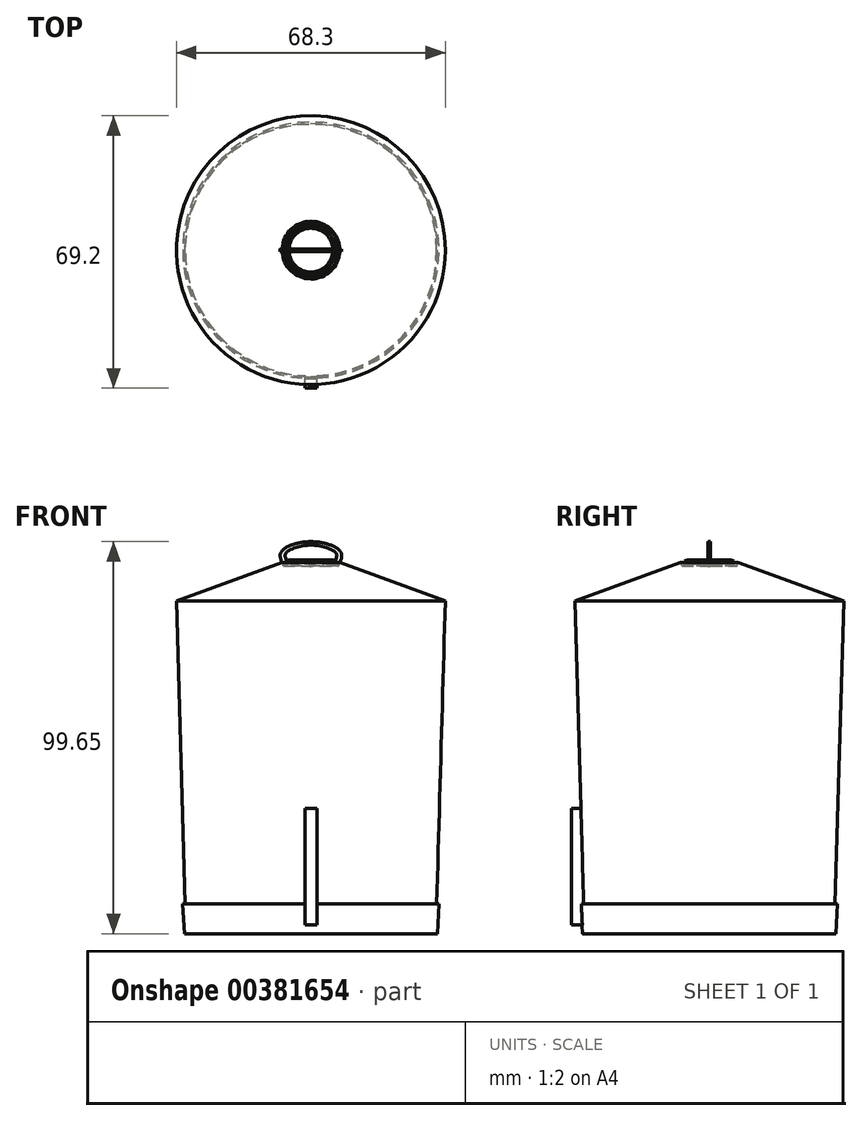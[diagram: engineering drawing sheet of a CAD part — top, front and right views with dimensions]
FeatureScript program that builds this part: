
annotation { "Feature Type Name" : "Feature", "Feature Type Description" : "" }
export const myFeature = defineFeature(function(context is Context, id is Id, definition is map)
    precondition{}
    {
        {
            var Q0;
            Q0=qCreatedBy(makeId("Front.planeOp"),FACE);
            var sketch = newSketch(context, id + "F0", { "sketchPlane" : qUnion([Q0])});
            skLineSegment(sketch, "E0", {"start": v(0, -43.36) * mm, "end": v(31.73, -43.36) * mm});
            skLineSegment(sketch, "E1", {"start": v(31.73, -43.36) * mm, "end": v(34.15, 41.18) * mm});
            skLineSegment(sketch, "E2", {"start": v(34.15, 41.18) * mm, "end": v(0, 41.18) * mm});
            skLineSegment(sketch, "E3", {"start": v(0, 53.72) * mm, "end": v(0, -61.04) * mm, "construction": true});
            skLineSegment(sketch, "E4", {"start": v(0, 41.18) * mm, "end": v(0, -43.36) * mm});
            skLineSegment(sketch, "E5", {"start": v(34.15, 41.18) * mm, "end": v(5.56, 51.68) * mm});
            skFitSpline(sketch, "E6", {"points": [v(5.56, 51.68) * mm, v(3.9, 50.72) * mm, v(1.74, 50.23) * mm, v(0, 50) * mm], "startDerivative": vector(-2.2, -3.08) * mm, "endDerivative": vector(-3.95, -0.4) * mm});
            skLineSegment(sketch, "E7", {"start": v(0, 50) * mm, "end": v(0, 41.18) * mm});
            skFitSpline(sketch, "E8", {"points": [v(6.25, 51.42) * mm, v(6.55, 53.07) * mm, v(5.64, 54.02) * mm, v(2.87, 55.06) * mm, v(0.6, 55.38) * mm, v(0, 55.38) * mm], "startDerivative": vector(2.99, 8.95) * mm, "endDerivative": vector(-4.23, -0.14) * mm});
            skFitSpline(sketch, "E9", {"points": [v(7.33, 51.03) * mm, v(7.82, 52.89) * mm, v(6.68, 54.56) * mm, v(4.78, 55.47) * mm, v(4.69, 55.47) * mm], "startDerivative": vector(2.68, 6.22) * mm, "endDerivative": vector(-0.9, -0.21) * mm});
            skFitSpline(sketch, "E10", {"points": [v(4.78, 55.47) * mm, v(2.83, 56.02) * mm, v(0, 56.29) * mm], "startDerivative": vector(-4.04, 1.35) * mm, "endDerivative": vector(-5.47, 0.32) * mm});
            skLineSegment(sketch, "E11", {"start": v(0, 55.38) * mm, "end": v(0, 56.29) * mm});
            skLineSegment(sketch, "E12", {"start": v(7.33, 51.03) * mm, "end": v(7, 50.14) * mm});
            skLineSegment(sketch, "E13", {"start": v(7, 50.14) * mm, "end": v(5.83, 50.57) * mm});
            skLineSegment(sketch, "E14", {"start": v(5.83, 50.57) * mm, "end": v(6.25, 51.42) * mm});
            skFitSpline(sketch, "E15.MirrorCS", {"points": [v(-6.25, 51.42) * mm, v(-6.55, 53.07) * mm, v(-5.64, 54.02) * mm, v(-2.87, 55.06) * mm, v(-0.6, 55.38) * mm, v(0, 55.38) * mm], "startDerivative": vector(-2.99, 8.95) * mm, "endDerivative": vector(4.23, -0.14) * mm});
            skFitSpline(sketch, "E16.MirrorCS", {"points": [v(-4.78, 55.47) * mm, v(-2.83, 56.02) * mm, v(0, 56.29) * mm], "startDerivative": vector(4.04, 1.35) * mm, "endDerivative": vector(5.47, 0.32) * mm});
            skFitSpline(sketch, "E17.MirrorCS", {"points": [v(-7.33, 51.03) * mm, v(-7.82, 52.89) * mm, v(-6.68, 54.56) * mm, v(-4.78, 55.47) * mm, v(-4.69, 55.47) * mm], "startDerivative": vector(-2.68, 6.22) * mm, "endDerivative": vector(0.9, -0.21) * mm});
            skLineSegment(sketch, "E18.MirrorCS", {"start": v(-7.33, 51.03) * mm, "end": v(-7, 50.14) * mm});
            skLineSegment(sketch, "E19.MirrorCS", {"start": v(-7, 50.14) * mm, "end": v(-5.83, 50.57) * mm});
            skLineSegment(sketch, "E20.MirrorCS", {"start": v(-5.83, 50.57) * mm, "end": v(-6.25, 51.42) * mm});
            skSolve(sketch);
        }
        {
            var Q0;
            Q0=makeQuery(id+"F0.imprint","IMPRINT",FACE,{"disambiguationData":[TD([[makeQuery(id+"F0.imprint","IMPRINT",EDGE,{"derivedFrom":sQuery(id+"F0.wireOp",EDGE,"E0")}),1.0]])]});
            var Q1;
            Q1=makeQuery(id+"F0.imprint","IMPRINT",FACE,{"disambiguationData":[TD([[makeQuery(id+"F0.imprint","IMPRINT",EDGE,{"derivedFrom":sQuery(id+"F0.wireOp",EDGE,"E2")}),-1.0]])]});
            var Q2;
            Q2=sQuery(id+"F0.wireOp",EDGE,"E3");
            revolve(context, id + "F1", {"entities" : qUnion([Q0, Q1]), "axis" : qUnion([Q2]), "revolveType" : RevolveType.FULL});
        }
        {
            var Q0;
            {var subQ1=sQuery(id+"F0.wireOp",EDGE,"E8");Q0=makeQuery(id+"F0.imprint","IMPRINT",FACE,{"disambiguationData":[TD([[makeQuery(id+"F0.imprint","IMPRINT",EDGE,{"derivedFrom":subQ1}),-1.0]])]});}
            var Q1;
            Q1=makeQuery(id+"F0.imprint","IMPRINT",FACE,{"disambiguationData":[TD([[makeQuery(id+"F0.imprint","IMPRINT",EDGE,{"derivedFrom":sQuery(id+"F0.wireOp",EDGE,"E11")}),1.0]])]});
            var Q2;
            {var subQ2=sQuery(id+"F0.wireOp",EDGE,"E12");Q2=makeQuery(id+"F0.imprint","IMPRINT",FACE,{"disambiguationData":[TD([[makeQuery(id+"F0.imprint","IMPRINT",EDGE,{"derivedFrom":subQ2}),-1.0]])]});}
            extrude(context, id + "F2", {"entities" : qUnion([Q0, Q1, Q2]), "operationType" : NewBodyOperationType.ADD, "endBound" : BoundingType.SYMMETRIC, "oppositeDirection" : true, "depth" : 0.64 * mm});
        }
        {
            var Q0;
            Q0=qCreatedBy(makeId("Front.planeOp"),FACE);
            cPlane(context, id + "F3", {"entities" : qUnion([Q0]), "cplaneType" : CPlaneType.OFFSET, "offset" : 31.75 * mm, "width" : 152.4 * mm, "height" : 152.4 * mm});
        }
        {
            var Q0;
            Q0=qCreatedBy(id+"F3.planeOp",FACE);
            var sketch = newSketch(context, id + "F4", { "sketchPlane" : qUnion([Q0])});
            skPoint(sketch, "E21.middle", {"position": v(0, -28.7) * mm});
            skPoint(sketch, "E21.top.end.orphan", {"position": v(1.51, -16.27) * mm});
            skPoint(sketch, "E21.top.start.orphan", {"position": v(-1.51, -16.27) * mm});
            skPoint(sketch, "E21.bottom.end.orphan", {"position": v(1.51, -41.11) * mm});
            skPoint(sketch, "E21.bottom.start.orphan", {"position": v(-1.51, -41.11) * mm});
            skLineSegment(sketch, "E22.bottom", {"start": v(-1.51, -41.11) * mm, "end": v(1.51, -41.11) * mm});
            skLineSegment(sketch, "E22.top", {"start": v(-1.51, -11.56) * mm, "end": v(1.51, -11.56) * mm});
            skLineSegment(sketch, "E22.left", {"start": v(-1.51, -41.11) * mm, "end": v(-1.51, -11.56) * mm});
            skLineSegment(sketch, "E22.right", {"start": v(1.51, -41.11) * mm, "end": v(1.51, -11.56) * mm});
            skPoint(sketch, "E22.middle", {"position": v(0, -26.34) * mm});
            skSolve(sketch);
        }
        {
            var Q0;
            Q0 = qSketchRegion(id + "F4", true);
            extrude(context, id + "F5", {"entities" : qUnion([Q0]), "operationType" : NewBodyOperationType.ADD, "depth" : 3.3 * mm});
        }
        {
            var Q0;
            Q0=makeQuery(id+"F1.opRevolve","SWEPT_FACE",FACE,{"disambiguationData":[OSD([sQuery(id+"F0.wireOp",EDGE,"E0")])]});
            var sketch = newSketch(context, id + "F6", { "sketchPlane" : qUnion([Q0])});
            skCircle(sketch, "E23", {"center": v(0, 0) * mm, "radius": 32.17 * mm});
            skSolve(sketch);
        }
        {
            var Q0;
            Q0 = qSketchRegion(id + "F6", true);
            extrude(context, id + "F7", {"entities" : qUnion([Q0]), "operationType" : NewBodyOperationType.ADD, "oppositeDirection" : true, "depth" : 7.62 * mm, "hasDraft" : true, "draftAngle" : 3 * degree});
        }
    });
